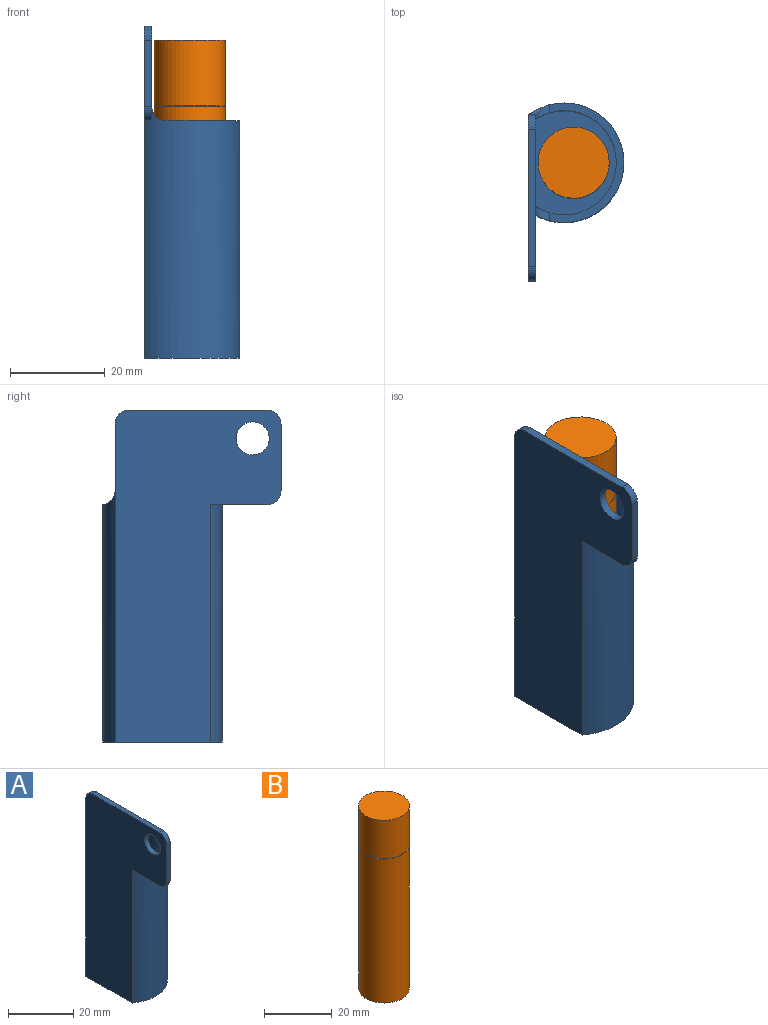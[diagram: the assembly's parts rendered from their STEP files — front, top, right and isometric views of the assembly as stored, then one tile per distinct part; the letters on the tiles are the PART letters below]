
ASSEMBLY  parts=2 mates=1
PART A: 18 faces, bbox 20.2x37.6x70 mm
  f0: cylinder r=12.6mm len=53mm, axis (0,0,-1), area 2800.8mm2, adj f1,f2,f4,f5,f8,f12,f13,f14
  f1: plane 70x35mm, normal (-1,0,0), area 1660.7mm2, adj f0,f2,f7,f8,f9,f10,f11,f15
  f2: plane 25.2x20.2mm, normal (0,0,-1), area 428.6mm2, adj f0,f1
  f3: cylinder r=11mm len=52mm, axis (0,0,-1), area 2319.7mm2, adj f4,f5,f6,f12,f14
  f4: plane 69x35mm, normal (1,0,0), area 1551.2mm2, adj f0,f3,f6,f7,f8,f9,f10,f11
  f5: plane 25.2x15.6mm, normal (0,0,1), area 69mm2, adj f0,f3,f12,f14
  f6: plane 22x17mm, normal (0,0,1), area 315.2mm2, adj f3,f4
  f7: plane 14x1.6mm, normal (0,1,0), area 22.4mm2, adj f1,f4,f13,f16
  f8: plane 11.9x1.6mm, normal (0,0,-1), area 18.2mm2, adj f0,f1,f4,f15
  f9: plane 14x1.6mm, normal (0,-1,0), area 22.4mm2, adj f1,f4,f15,f17
  f10: plane 29x1.6mm, normal (0,0,1), area 46.4mm2, adj f1,f4,f16,f17
  f11: cylinder r=3.5mm len=7mm, axis (-1,0,0), area 35.2mm2, adj f1,f4
  f12: cylinder r=3mm len=3.02mm, axis (0,1,0), area 8.3mm2, adj f0,f3,f4,f5
  f13: cylinder r=3mm len=3.45mm, axis (-1,0,0), area 4.3mm2, adj f0,f7,f14
  f14: cylinder r=3mm len=3.02mm, axis (0,1,0), area 5.9mm2, adj f0,f3,f4,f5,f13
  f15: cylinder r=3mm len=3mm, axis (-1,0,0), area 7.5mm2, adj f1,f4,f8,f9
  f16: cylinder r=3mm len=3mm, axis (-1,0,0), area 7.5mm2, adj f1,f4,f7,f10
  f17: cylinder r=3mm len=3mm, axis (1,0,0), area 7.5mm2, adj f1,f4,f9,f10
PART B: 7 faces, bbox 15x15x66 mm
  f0: cylinder r=7.5mm len=15mm, axis (0,0,-1), area 650.3mm2, adj f1,f3
  f1: plane 15x15mm, normal (0,0,1), area 176.7mm2, adj f0
  f2: cylinder r=7.3mm len=14.6mm, axis (0,0,-1), area 9.2mm2, adj f3,f4
  f3: plane 15x15mm, normal (0,0,-1), area 9.3mm2, adj f0,f2
  f4: plane 15x15mm, normal (0,0,1), area 9.3mm2, adj f2,f6
  f5: plane 15x15mm, normal (0,0,-1), area 176.7mm2, adj f6
  f6: cylinder r=7.5mm len=52mm, axis (0,0,-1), area 2450.4mm2, adj f4,f5
PLACE A t=(0,0,-1)mm
PLACE B rot(axis=(0,0,1),0deg) t=(2,0,0)mm
MATE slider A.f3 <-> B.f5  axis (0,0,1) through (0,0,0)mm
